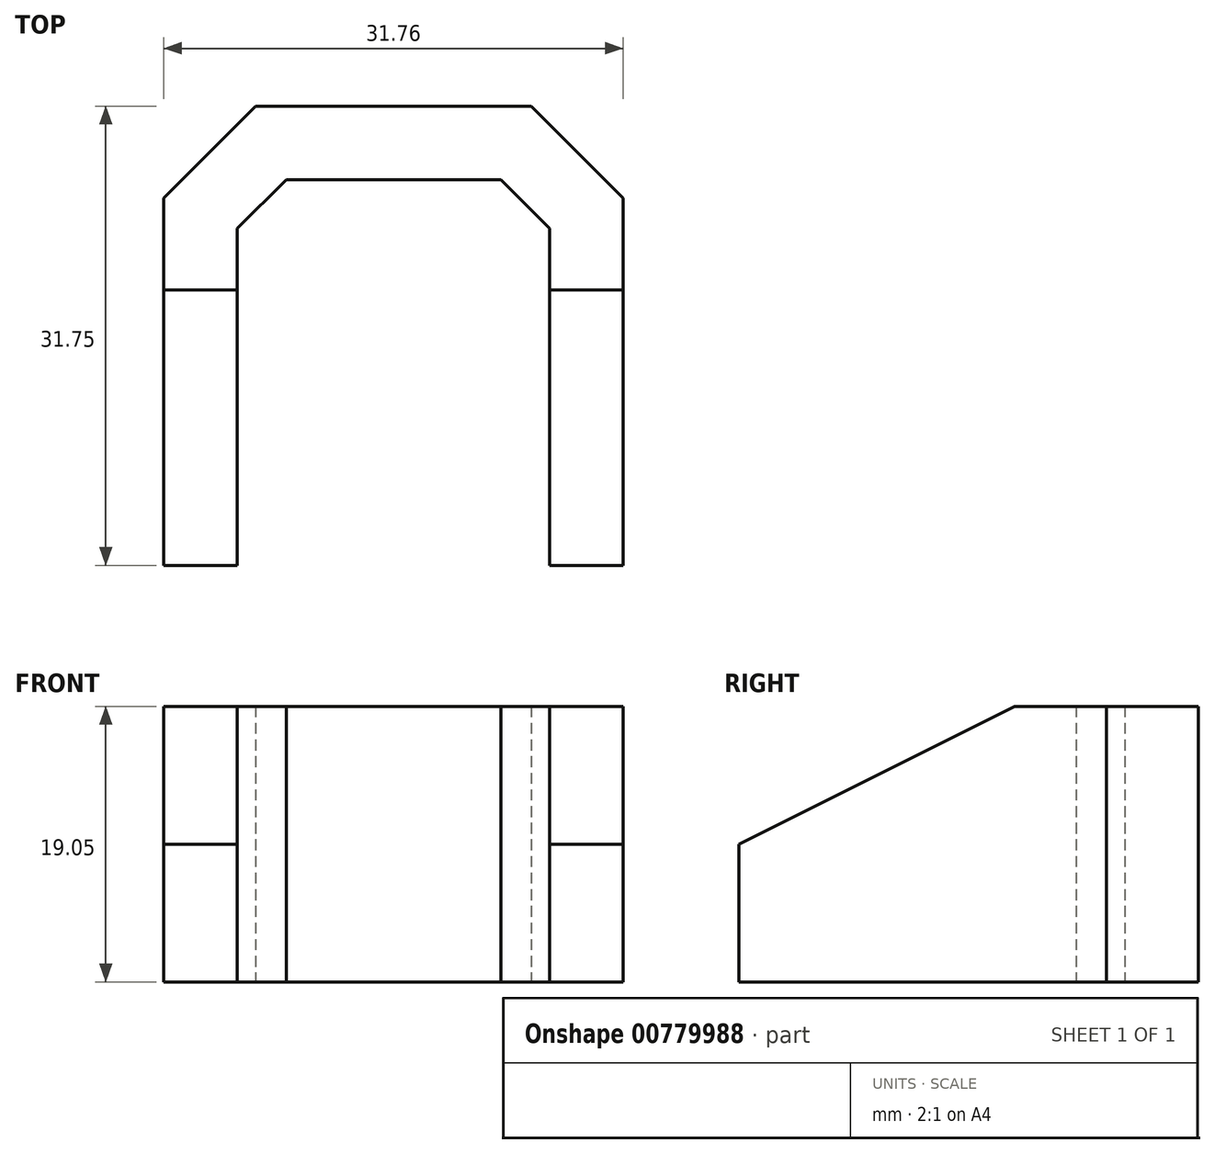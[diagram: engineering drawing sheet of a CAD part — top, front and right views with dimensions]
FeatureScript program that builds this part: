
annotation { "Feature Type Name" : "Feature", "Feature Type Description" : "" }
export const myFeature = defineFeature(function(context is Context, id is Id, definition is map)
    precondition{}
    {
        {
            var Q0;
            Q0=qCreatedBy(makeId("Top.planeOp"),FACE);
            var sketch = newSketch(context, id + "F0", { "sketchPlane" : qUnion([Q0])});
            skLineSegment(sketch, "E0", {"start": v(-15.87, 0) * mm, "end": v(15.87, 0) * mm});
            skLineSegment(sketch, "E1", {"start": v(15.88, 0) * mm, "end": v(15.88, 25.4) * mm});
            skLineSegment(sketch, "E2", {"start": v(15.88, 25.4) * mm, "end": v(9.52, 31.75) * mm});
            skLineSegment(sketch, "E3", {"start": v(9.52, 31.75) * mm, "end": v(-9.53, 31.75) * mm});
            skLineSegment(sketch, "E4", {"start": v(-9.52, 31.75) * mm, "end": v(-15.88, 25.4) * mm});
            skLineSegment(sketch, "E5", {"start": v(-15.88, 25.4) * mm, "end": v(-15.88, 0) * mm});
            skSolve(sketch);
        }
        {
            var Q0;
            Q0 = qSketchRegion(id + "F0", true);
            extrude(context, id + "F1", {"entities" : qUnion([Q0]), "depth" : 19.05 * mm, "offsetDistance" : 25.4 * mm});
        }
        {
            var Q0;
            Q0=makeQuery(id+"F1.opExtrude","CAP_FACE",FACE,{"disambiguationData":[OSD([sQuery(id+"F0.wireOp",EDGE,"E0"),sQuery(id+"F0.wireOp",EDGE,"E1"),sQuery(id+"F0.wireOp",EDGE,"E2"),sQuery(id+"F0.wireOp",EDGE,"E3"),sQuery(id+"F0.wireOp",EDGE,"E4"),sQuery(id+"F0.wireOp",EDGE,"E5")])],"isStart":false});
            var Q1;
            Q1=makeQuery(id+"F1.opExtrude","SWEPT_FACE",FACE,{"disambiguationData":[OSD([sQuery(id+"F0.wireOp",EDGE,"E0")])]});
            var Q2;
            Q2=makeQuery(id+"F1.opExtrude","CAP_FACE",FACE,{"disambiguationData":[OSD([sQuery(id+"F0.wireOp",EDGE,"E0"),sQuery(id+"F0.wireOp",EDGE,"E1"),sQuery(id+"F0.wireOp",EDGE,"E2"),sQuery(id+"F0.wireOp",EDGE,"E3"),sQuery(id+"F0.wireOp",EDGE,"E4"),sQuery(id+"F0.wireOp",EDGE,"E5")])],"isStart":true});
            shell(context, id + "F2", {"entities" : qUnion([Q0, Q1, Q2]), "thickness" : 5.08 * mm});
        }
        {
            var Q0;
            Q0=makeQuery(id+"F1.opExtrude","SWEPT_FACE",FACE,{"disambiguationData":[OSD([sQuery(id+"F0.wireOp",EDGE,"E1")])]});
            var sketch = newSketch(context, id + "F3", { "sketchPlane" : qUnion([Q0])});
            skLineSegment(sketch, "E6", {"start": v(0, 9.53) * mm, "end": v(19.05, 19.05) * mm});
            skLineSegment(sketch, "E7", {"start": v(19.05, 19.05) * mm, "end": v(0, 19.05) * mm});
            skLineSegment(sketch, "E8", {"start": v(0, 19.05) * mm, "end": v(0, 9.53) * mm});
            skSolve(sketch);
        }
        {
            var Q0;
            Q0=makeQuery(id+"F3.imprint","IMPRINT",FACE,{"disambiguationData":[TD([[makeQuery(id+"F3.imprint","IMPRINT",EDGE,{"derivedFrom":sQuery(id+"F3.wireOp",EDGE,"E6")}),1.0]])]});
            extrude(context, id + "F4", {"entities" : qUnion([Q0]), "operationType" : NewBodyOperationType.REMOVE, "endBound" : BoundingType.THROUGH_ALL, "oppositeDirection" : true, "depth" : 25.4 * mm, "offsetDistance" : 25.4 * mm});
        }
    });
